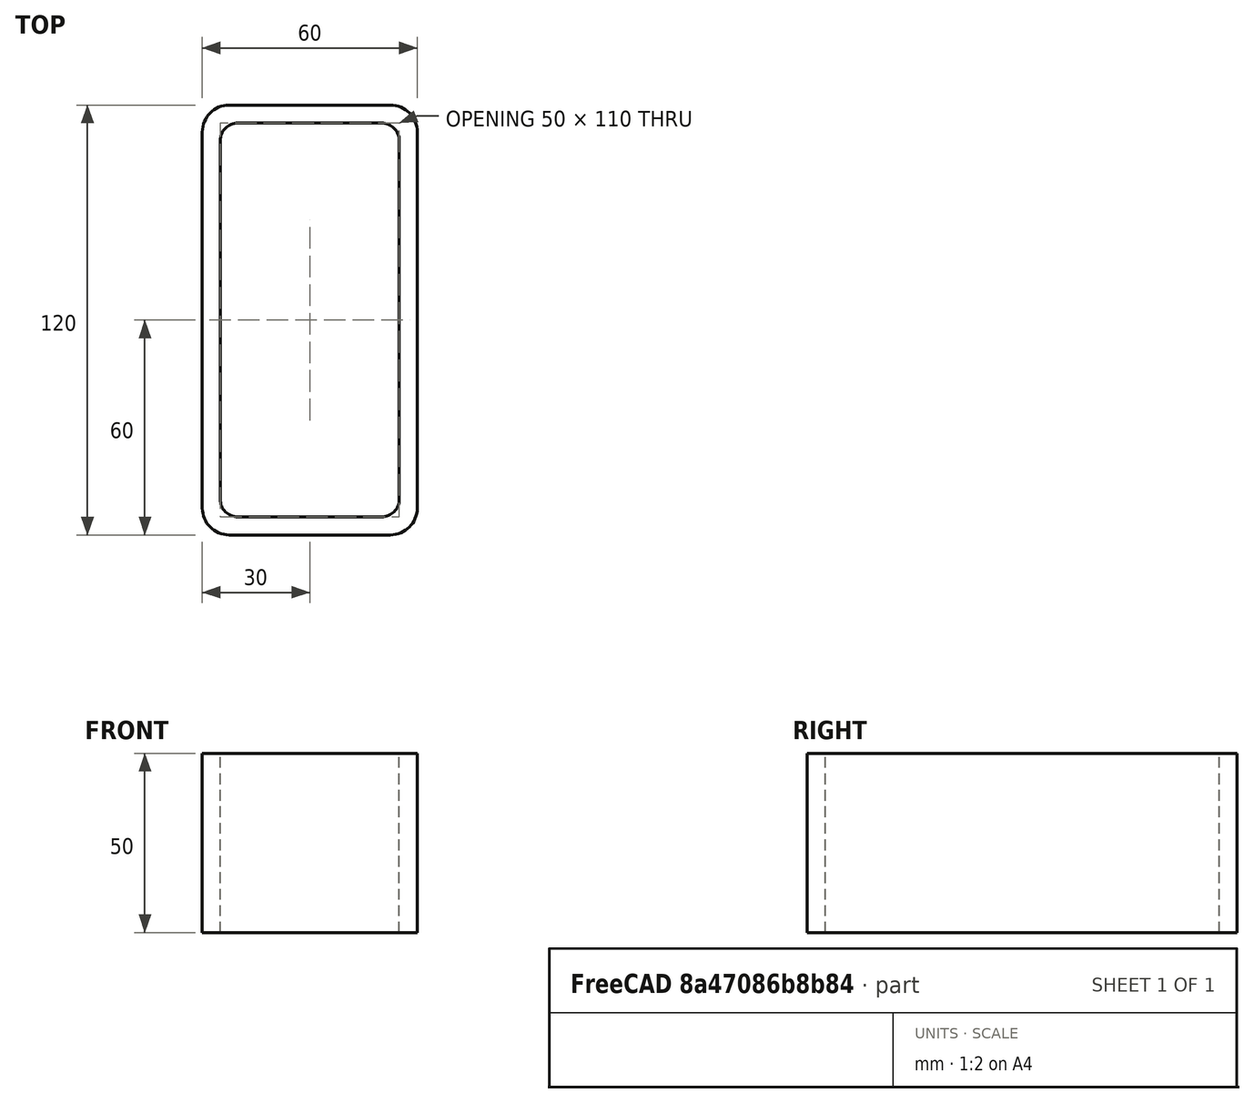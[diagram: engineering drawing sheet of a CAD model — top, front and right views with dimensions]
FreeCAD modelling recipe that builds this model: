
FCSTD DOCUMENT  (FreeCAD 0.15R4671 (Git))
Label: Rectangular hollow section 120x60x5 EN10219 S235JRH
License: All rights reserved
LicenseURL: http://en.wikipedia.org/wiki/All_rights_reserved
objects: Sketcher::SketchObject×1, Part::Extrusion×1
note: 2 computed .brp shape members not serialized (recipe doc carries the construction recipe); baked Part::Feature solids carry a one-line shape summary decoded from their .brp

FEATURE [Sketcher::SketchObject] Sketch
  sketch-geometry (16):
    g0: LineSegment StartX=-20 StartY=55 StartZ=0 EndX=20 EndY=55 EndZ=0
    g1: LineSegment StartX=25 StartY=50 StartZ=0 EndX=25 EndY=-50 EndZ=0
    g2: LineSegment StartX=20 StartY=-55 StartZ=0 EndX=-20 EndY=-55 EndZ=0
    g3: LineSegment StartX=-25 StartY=-50 StartZ=0 EndX=-25 EndY=50 EndZ=0
    g4: LineSegment StartX=-22.5 StartY=60 StartZ=0 EndX=22.5 EndY=60 EndZ=0
    g5: LineSegment StartX=30 StartY=52.5 StartZ=0 EndX=30 EndY=-52.5 EndZ=0
    g6: LineSegment StartX=22.5 StartY=-60 StartZ=0 EndX=-22.5 EndY=-60 EndZ=0
    g7: LineSegment StartX=-30 StartY=-52.5 StartZ=0 EndX=-30 EndY=52.5 EndZ=0
    g8: ArcOfCircle CenterX=-20 CenterY=50 CenterZ=0 NormalX=0 NormalY=0 NormalZ=1 Radius=5 StartAngle=1.5708 EndAngle=3.14159
    g9: ArcOfCircle CenterX=20 CenterY=50 CenterZ=0 NormalX=0 NormalY=0 NormalZ=1 Radius=5 StartAngle=0 EndAngle=1.5708
    g10: ArcOfCircle CenterX=20 CenterY=-50 CenterZ=0 NormalX=0 NormalY=0 NormalZ=1 Radius=5 StartAngle=4.71239 EndAngle=6.28319
    g11: ArcOfCircle CenterX=-20 CenterY=-50 CenterZ=0 NormalX=0 NormalY=0 NormalZ=1 Radius=5 StartAngle=3.14159 EndAngle=4.71239
    g12: ArcOfCircle CenterX=22.5 CenterY=52.5 CenterZ=0 NormalX=0 NormalY=0 NormalZ=1 Radius=7.5 StartAngle=0 EndAngle=1.5708
    g13: ArcOfCircle CenterX=22.5 CenterY=-52.5 CenterZ=0 NormalX=0 NormalY=0 NormalZ=1 Radius=7.5 StartAngle=4.71239 EndAngle=6.28319
    g14: ArcOfCircle CenterX=-22.5 CenterY=-52.5 CenterZ=0 NormalX=0 NormalY=0 NormalZ=1 Radius=7.5 StartAngle=3.14159 EndAngle=4.71239
    g15: ArcOfCircle CenterX=-22.5 CenterY=52.5 CenterZ=0 NormalX=0 NormalY=0 NormalZ=1 Radius=7.5 StartAngle=1.5708 EndAngle=3.14159
  constraints (36):
    c: Horizontal(g2)
    c: Vertical(g3)
    c: Horizontal(g6)
    c: Vertical(g7)
    c: Tangent(g3,g8) = 1.5708
    c: Tangent(g0,g8) = 1.5708
    c: Tangent(g0,g9) = 1.5708
    c: Tangent(g1,g9) = 1.5708
    c: Tangent(g1,g10) = 1.5708
    c: Tangent(g2,g10) = 1.5708
    c: Tangent(g2,g11) = 1.5708
    c: Tangent(g3,g11) = 1.5708
    c: Tangent(g4,g12) = 1.5708
    c: Tangent(g5,g12) = 1.5708
    c: Tangent(g5,g13) = 1.5708
    c: Tangent(g6,g13) = 1.5708
    c: Tangent(g6,g14) = 1.5708
    c: Tangent(g7,g14) = 1.5708
    c: Tangent(g7,g15) = 1.5708
    c: Tangent(g4,g15) = 1.5708
    c: Equal(g9,g8)
    c: Equal(g9,g11)
    c: Equal(g9,g10)
    c: Equal(g12,g15)
    c: Equal(g12,g14)
    c: Equal(g12,g13)
    c: Symmetric(g4,g6,g-1)
    c: Symmetric(g7,g5,g-2)
    c: DistanceY(g4,g6) = -120
    c: DistanceX(g7,g5) = 60
    c: Symmetric(g3,g1,g-2)
    c: Symmetric(g0,g2,g-1)
    c: DistanceY(g0,g4) = 5
    c: DistanceX(g5,g1) = -5
    c: Radius(g9) = 5
    c: Radius(g12) = 7.5
FEATURE [Part::Extrusion] Extrude  label="Rectangular hollow section 120x60x5 EN10219 S235JRH"
  Base = -> Sketch
  Dir = (0,0,50)
  Solid = true
